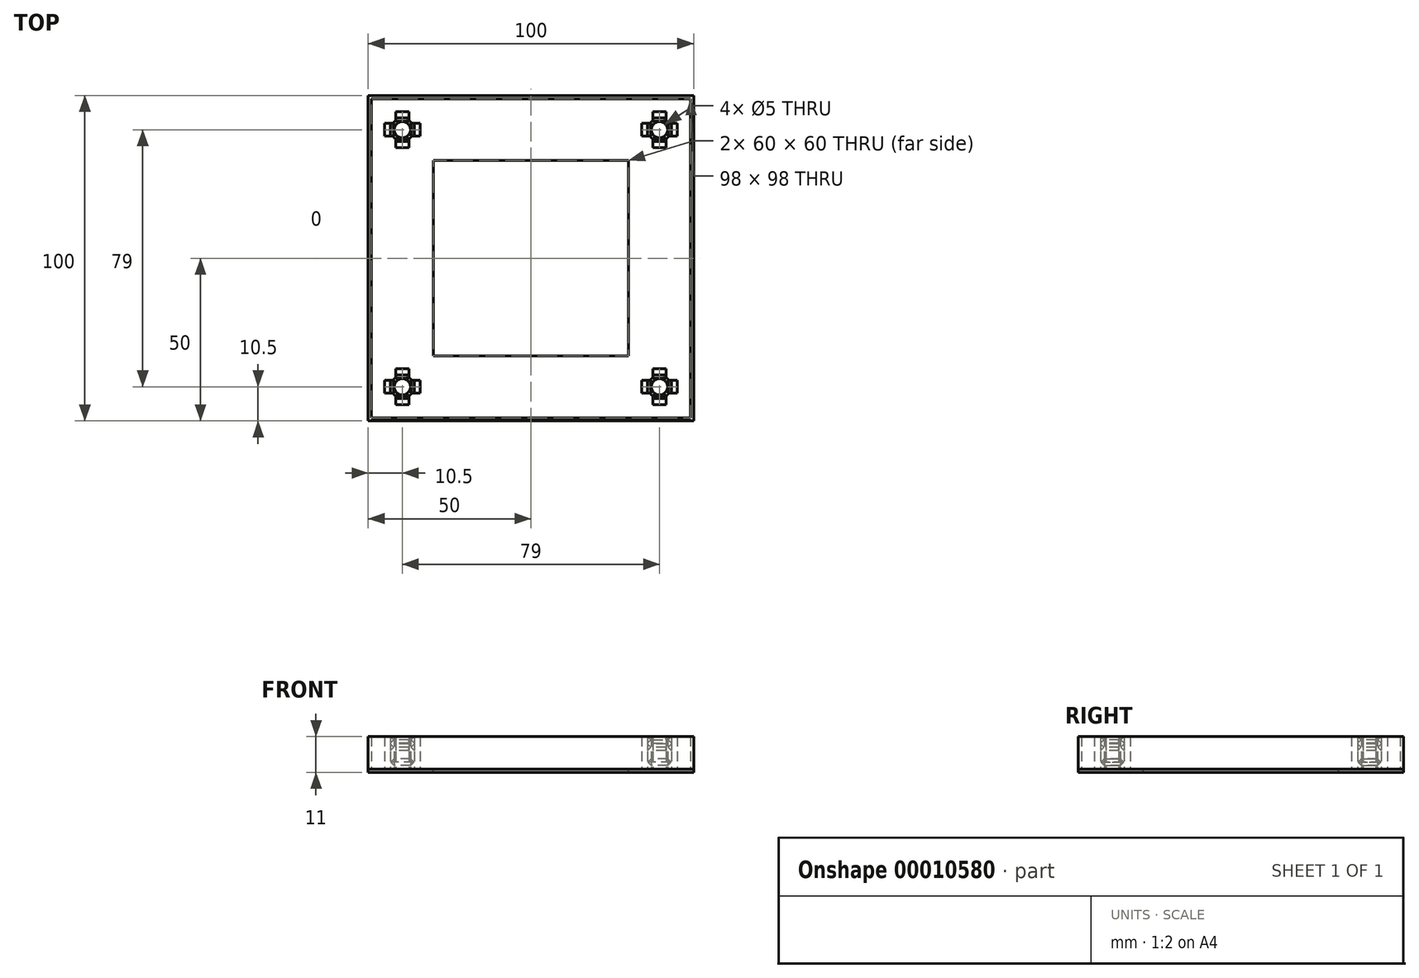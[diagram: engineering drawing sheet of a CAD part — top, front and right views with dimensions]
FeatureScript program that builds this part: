
annotation { "Feature Type Name" : "Feature", "Feature Type Description" : "" }
export const myFeature = defineFeature(function(context is Context, id is Id, definition is map)
    precondition{}
    {
        {
            var Q0;
            Q0=qCreatedBy(makeId("Top.planeOp"),FACE);
            var sketch = newSketch(context, id + "F0", { "sketchPlane" : qUnion([Q0])});
            skLineSegment(sketch, "E0.bottom", {"start": v(-50, 50) * mm, "end": v(50, 50) * mm});
            skLineSegment(sketch, "E0.top", {"start": v(-50, -50) * mm, "end": v(50, -50) * mm});
            skLineSegment(sketch, "E0.left", {"start": v(-50, 50) * mm, "end": v(-50, -50) * mm});
            skLineSegment(sketch, "E0.right", {"start": v(50, 50) * mm, "end": v(50, -50) * mm});
            skCircle(sketch, "E1", {"center": v(-39.5, -39.5) * mm, "radius": 2.5 * mm});
            skCircle(sketch, "E2", {"center": v(-39.5, -39.5) * mm, "radius": 3.5 * mm});
            skLineSegment(sketch, "E3.0", {"start": v(-49, 49) * mm, "end": v(-49, -49) * mm});
            skLineSegment(sketch, "E3.1", {"start": v(-49, 49) * mm, "end": v(49, 49) * mm});
            skLineSegment(sketch, "E3.2", {"start": v(49, 49) * mm, "end": v(49, -49) * mm});
            skLineSegment(sketch, "E3.3", {"start": v(-49, -49) * mm, "end": v(49, -49) * mm});
            skLineSegment(sketch, "E4.0", {"start": v(-30, 30) * mm, "end": v(-30, -30) * mm});
            skLineSegment(sketch, "E4.1", {"start": v(-30, 30) * mm, "end": v(30, 30) * mm});
            skLineSegment(sketch, "E4.2", {"start": v(30, 30) * mm, "end": v(30, -30) * mm});
            skLineSegment(sketch, "E4.3", {"start": v(-30, -30) * mm, "end": v(30, -30) * mm});
            skLineSegment(sketch, "E5", {"start": v(-30, -30) * mm, "end": v(-49, -49) * mm, "construction": true});
            skCircle(sketch, "E6.1.0", {"center": v(39.5, -39.5) * mm, "radius": 2.5 * mm});
            skCircle(sketch, "E6.1.1", {"center": v(39.5, -39.5) * mm, "radius": 3.5 * mm});
            skCircle(sketch, "E6.2.0", {"center": v(39.5, 39.5) * mm, "radius": 2.5 * mm});
            skCircle(sketch, "E6.2.1", {"center": v(39.5, 39.5) * mm, "radius": 3.5 * mm});
            skCircle(sketch, "E6.3.0", {"center": v(-39.5, 39.5) * mm, "radius": 2.5 * mm});
            skCircle(sketch, "E6.3.1", {"center": v(-39.5, 39.5) * mm, "radius": 3.5 * mm});
            skPoint(sketch, "E6.center", {"position": v(0, 0) * mm});
            skSolve(sketch);
        }
        {
            var Q0;
            Q0=makeQuery(id+"F0.imprint","IMPRINT",FACE,{"disambiguationData":[TD([[makeQuery(id+"F0.imprint","IMPRINT",EDGE,{"derivedFrom":sQuery(id+"F0.wireOp",EDGE,"E1")}),1.0]])]});
            var Q1;
            Q1=makeQuery(id+"F0.imprint","IMPRINT",FACE,{"disambiguationData":[TD([[makeQuery(id+"F0.imprint","IMPRINT",EDGE,{"derivedFrom":sQuery(id+"F0.wireOp",EDGE,"E6.3.0")}),1.0]])]});
            var Q2;
            Q2=makeQuery(id+"F0.imprint","IMPRINT",FACE,{"disambiguationData":[TD([[makeQuery(id+"F0.imprint","IMPRINT",EDGE,{"derivedFrom":sQuery(id+"F0.wireOp",EDGE,"E6.2.0")}),1.0]])]});
            var Q3;
            Q3=makeQuery(id+"F0.imprint","IMPRINT",FACE,{"disambiguationData":[TD([[makeQuery(id+"F0.imprint","IMPRINT",EDGE,{"derivedFrom":sQuery(id+"F0.wireOp",EDGE,"E6.1.0")}),1.0]])]});
            extrude(context, id + "F1", {"entities" : qUnion([Q0, Q1, Q2, Q3]), "depth" : 10 * mm});
        }
        {
            var Q0;
            Q0=makeQuery(id+"F0.imprint","IMPRINT",FACE,{"disambiguationData":[TD([[makeQuery(id+"F0.imprint","IMPRINT",EDGE,{"derivedFrom":sQuery(id+"F0.wireOp",EDGE,"E1")}),-1.0]])]});
            var Q1;
            Q1=makeQuery(id+"F0.imprint","IMPRINT",FACE,{"disambiguationData":[TD([[makeQuery(id+"F0.imprint","IMPRINT",EDGE,{"derivedFrom":sQuery(id+"F0.wireOp",EDGE,"E6.3.0")}),-1.0]])]});
            var Q2;
            Q2=makeQuery(id+"F0.imprint","IMPRINT",FACE,{"disambiguationData":[TD([[makeQuery(id+"F0.imprint","IMPRINT",EDGE,{"derivedFrom":sQuery(id+"F0.wireOp",EDGE,"E6.2.0")}),-1.0]])]});
            var Q3;
            Q3=makeQuery(id+"F0.imprint","IMPRINT",FACE,{"disambiguationData":[TD([[makeQuery(id+"F0.imprint","IMPRINT",EDGE,{"derivedFrom":sQuery(id+"F0.wireOp",EDGE,"E6.1.0")}),-1.0]])]});
            extrude(context, id + "F2", {"entities" : qUnion([Q0, Q1, Q2, Q3]), "depth" : 3.15 * mm, "hasSecondDirection" : true, "secondDirectionOppositeDirection" : false, "secondDirectionDepth" : 1.15 * mm});
        }
        {
            var Q0;
            Q0=makeQuery(id+"F2.opExtrude","CAP_EDGE",EDGE,{"disambiguationData":[OSD([sQuery(id+"F0.wireOp",EDGE,"E2")])],"isStart":false});
            var Q1;
            Q1=makeQuery(id+"F2.opExtrude","CAP_EDGE",EDGE,{"disambiguationData":[OSD([sQuery(id+"F0.wireOp",EDGE,"E2")])],"isStart":true});
            var Q2;
            Q2=makeQuery(id+"F2.opExtrude","CAP_EDGE",EDGE,{"disambiguationData":[OSD([sQuery(id+"F0.wireOp",EDGE,"E6.1.1")])],"isStart":true});
            var Q3;
            Q3=makeQuery(id+"F2.opExtrude","CAP_EDGE",EDGE,{"disambiguationData":[OSD([sQuery(id+"F0.wireOp",EDGE,"E6.1.1")])],"isStart":false});
            var Q4;
            Q4=makeQuery(id+"F2.opExtrude","CAP_EDGE",EDGE,{"disambiguationData":[OSD([sQuery(id+"F0.wireOp",EDGE,"E6.3.1")])],"isStart":true});
            var Q5;
            Q5=makeQuery(id+"F2.opExtrude","CAP_EDGE",EDGE,{"disambiguationData":[OSD([sQuery(id+"F0.wireOp",EDGE,"E6.3.1")])],"isStart":false});
            var Q6;
            Q6=makeQuery(id+"F2.opExtrude","CAP_EDGE",EDGE,{"disambiguationData":[OSD([sQuery(id+"F0.wireOp",EDGE,"E6.2.1")])],"isStart":true});
            var Q7;
            Q7=makeQuery(id+"F2.opExtrude","CAP_EDGE",EDGE,{"disambiguationData":[OSD([sQuery(id+"F0.wireOp",EDGE,"E6.2.1")])],"isStart":false});
            chamfer(context, id + "F3", {"entities" : qUnion([Q0, Q1, Q2, Q3, Q4, Q5, Q6, Q7]), "width" : 1 * mm, "tangentPropagation" : true});
        }
        {
            var Q0;
            Q0=makeQuery(id+"F0.imprint","IMPRINT",FACE,{"disambiguationData":[TD([[makeQuery(id+"F0.imprint","IMPRINT",EDGE,{"derivedFrom":sQuery(id+"F0.wireOp",EDGE,"E0.bottom")}),-1.0]])]});
            var Q1;
            Q1=makeQuery(id+"F0.imprint","IMPRINT",FACE,{"disambiguationData":[TD([[makeQuery(id+"F0.imprint","IMPRINT",EDGE,{"derivedFrom":sQuery(id+"F0.wireOp",EDGE,"E1")}),1.0]])]});
            extrude(context, id + "F4", {"entities" : qUnion([Q0, Q1]), "depth" : 10 * mm});
        }
        {
            var Q0;
            Q0=qCreatedBy(makeId("Top.planeOp"),FACE);
            var sketch = newSketch(context, id + "F5", { "sketchPlane" : qUnion([Q0])});
            skLineSegment(sketch, "E7.bottom", {"start": v(50, 50) * mm, "end": v(-50, 50) * mm});
            skLineSegment(sketch, "E7.top", {"start": v(50, -50) * mm, "end": v(-50, -50) * mm});
            skLineSegment(sketch, "E7.left", {"start": v(50, 50) * mm, "end": v(50, -50) * mm});
            skLineSegment(sketch, "E7.right", {"start": v(-50, 50) * mm, "end": v(-50, -50) * mm});
            skLineSegment(sketch, "E8.bottom", {"start": v(-41.5, -34) * mm, "end": v(-37.5, -34) * mm});
            skLineSegment(sketch, "E8.top", {"start": v(-41.5, -37) * mm, "end": v(-37.5, -37) * mm});
            skLineSegment(sketch, "E8.left", {"start": v(-41.5, -34) * mm, "end": v(-41.5, -37) * mm});
            skLineSegment(sketch, "E8.right", {"start": v(-37.5, -34) * mm, "end": v(-37.5, -37) * mm});
            skPoint(sketch, "E9", {"position": v(-39.5, -39.5) * mm});
            skCircle(sketch, "E10", {"center": v(-39.5, -39.5) * mm, "radius": 2.5 * mm, "construction": true});
            skLineSegment(sketch, "E11", {"start": v(-39.5, -39.5) * mm, "end": v(-39.5, -34) * mm, "construction": true});
            skLineSegment(sketch, "E12.1.0", {"start": v(-42, -41.5) * mm, "end": v(-42, -37.5) * mm});
            skLineSegment(sketch, "E12.1.1", {"start": v(-45, -41.5) * mm, "end": v(-45, -37.5) * mm});
            skLineSegment(sketch, "E12.1.2", {"start": v(-45, -37.5) * mm, "end": v(-42, -37.5) * mm});
            skLineSegment(sketch, "E12.1.3", {"start": v(-45, -41.5) * mm, "end": v(-42, -41.5) * mm});
            skLineSegment(sketch, "E12.2.0", {"start": v(-37.5, -42) * mm, "end": v(-41.5, -42) * mm});
            skLineSegment(sketch, "E12.2.1", {"start": v(-37.5, -45) * mm, "end": v(-41.5, -45) * mm});
            skLineSegment(sketch, "E12.2.2", {"start": v(-41.5, -45) * mm, "end": v(-41.5, -42) * mm});
            skLineSegment(sketch, "E12.2.3", {"start": v(-37.5, -45) * mm, "end": v(-37.5, -42) * mm});
            skLineSegment(sketch, "E12.3.0", {"start": v(-37, -37.5) * mm, "end": v(-37, -41.5) * mm});
            skLineSegment(sketch, "E12.3.1", {"start": v(-34, -37.5) * mm, "end": v(-34, -41.5) * mm});
            skLineSegment(sketch, "E12.3.2", {"start": v(-34, -41.5) * mm, "end": v(-37, -41.5) * mm});
            skLineSegment(sketch, "E12.3.3", {"start": v(-34, -37.5) * mm, "end": v(-37, -37.5) * mm});
            skLineSegment(sketch, "E13", {"start": v(-37.5, -35.85) * mm, "end": v(-41.5, -35.85) * mm});
            skLineSegment(sketch, "E14.1.0", {"start": v(-43.15, -37.5) * mm, "end": v(-43.15, -41.5) * mm});
            skLineSegment(sketch, "E14.2.0", {"start": v(-41.5, -43.15) * mm, "end": v(-37.5, -43.15) * mm});
            skLineSegment(sketch, "E14.3.0", {"start": v(-35.85, -41.5) * mm, "end": v(-35.85, -37.5) * mm});
            skLineSegment(sketch, "E15", {"start": v(-41.5, -36.85) * mm, "end": v(-37.5, -36.85) * mm});
            skLineSegment(sketch, "E16.1.0", {"start": v(-42.15, -41.5) * mm, "end": v(-42.15, -37.5) * mm});
            skLineSegment(sketch, "E16.2.0", {"start": v(-37.5, -42.15) * mm, "end": v(-41.5, -42.15) * mm});
            skLineSegment(sketch, "E16.3.0", {"start": v(-36.85, -37.5) * mm, "end": v(-36.85, -41.5) * mm});
            skPoint(sketch, "E17.1.0", {"position": v(39.5, -39.5) * mm});
            skLineSegment(sketch, "E17.1.1", {"start": v(41.5, -45) * mm, "end": v(37.5, -45) * mm});
            skLineSegment(sketch, "E17.1.2", {"start": v(37, -41.5) * mm, "end": v(37, -37.5) * mm});
            skLineSegment(sketch, "E17.1.3", {"start": v(37.5, -37) * mm, "end": v(41.5, -37) * mm});
            skLineSegment(sketch, "E17.1.4", {"start": v(35.85, -37.5) * mm, "end": v(35.85, -41.5) * mm});
            skLineSegment(sketch, "E17.1.5", {"start": v(45, -41.5) * mm, "end": v(42, -41.5) * mm});
            skLineSegment(sketch, "E17.1.6", {"start": v(37.5, -34) * mm, "end": v(37.5, -37) * mm});
            skLineSegment(sketch, "E17.1.7", {"start": v(34, -41.5) * mm, "end": v(34, -37.5) * mm});
            skLineSegment(sketch, "E17.1.8", {"start": v(41.5, -45) * mm, "end": v(41.5, -42) * mm});
            skLineSegment(sketch, "E17.1.9", {"start": v(37.5, -36.85) * mm, "end": v(41.5, -36.85) * mm});
            skLineSegment(sketch, "E17.1.10", {"start": v(34, -37.5) * mm, "end": v(37, -37.5) * mm});
            skLineSegment(sketch, "E17.1.11", {"start": v(45, -37.5) * mm, "end": v(45, -41.5) * mm});
            skLineSegment(sketch, "E17.1.12", {"start": v(36.85, -41.5) * mm, "end": v(36.85, -37.5) * mm});
            skLineSegment(sketch, "E17.1.13", {"start": v(45, -37.5) * mm, "end": v(42, -37.5) * mm});
            skLineSegment(sketch, "E17.1.14", {"start": v(43.15, -41.5) * mm, "end": v(43.15, -37.5) * mm});
            skLineSegment(sketch, "E17.1.15", {"start": v(34, -41.5) * mm, "end": v(37, -41.5) * mm});
            skCircle(sketch, "E17.1.16", {"center": v(39.5, -39.5) * mm, "radius": 2.5 * mm, "construction": true});
            skLineSegment(sketch, "E17.1.17", {"start": v(41.5, -42) * mm, "end": v(37.5, -42) * mm});
            skLineSegment(sketch, "E17.1.18", {"start": v(42.15, -37.5) * mm, "end": v(42.15, -41.5) * mm});
            skLineSegment(sketch, "E17.1.19", {"start": v(39.5, -39.5) * mm, "end": v(34, -39.5) * mm, "construction": true});
            skLineSegment(sketch, "E17.1.20", {"start": v(37.5, -43.15) * mm, "end": v(41.5, -43.15) * mm});
            skLineSegment(sketch, "E17.1.21", {"start": v(41.5, -42.15) * mm, "end": v(37.5, -42.15) * mm});
            skLineSegment(sketch, "E17.1.22", {"start": v(37.5, -34) * mm, "end": v(41.5, -34) * mm});
            skLineSegment(sketch, "E17.1.23", {"start": v(42, -37.5) * mm, "end": v(42, -41.5) * mm});
            skLineSegment(sketch, "E17.1.24", {"start": v(37.5, -45) * mm, "end": v(37.5, -42) * mm});
            skLineSegment(sketch, "E17.1.25", {"start": v(41.5, -34) * mm, "end": v(41.5, -37) * mm});
            skLineSegment(sketch, "E17.1.26", {"start": v(41.5, -35.85) * mm, "end": v(37.5, -35.85) * mm});
            skPoint(sketch, "E17.1.27", {"position": v(39.5, -39.5) * mm});
            skPoint(sketch, "E17.1.28", {"position": v(39.5, -39.5) * mm});
            skPoint(sketch, "E17.1.29", {"position": v(39.5, -39.5) * mm});
            skPoint(sketch, "E17.2.0", {"position": v(39.5, 39.5) * mm});
            skLineSegment(sketch, "E17.2.1", {"start": v(45, 41.5) * mm, "end": v(45, 37.5) * mm});
            skLineSegment(sketch, "E17.2.2", {"start": v(41.5, 37) * mm, "end": v(37.5, 37) * mm});
            skLineSegment(sketch, "E17.2.3", {"start": v(37, 37.5) * mm, "end": v(37, 41.5) * mm});
            skLineSegment(sketch, "E17.2.4", {"start": v(37.5, 35.85) * mm, "end": v(41.5, 35.85) * mm});
            skLineSegment(sketch, "E17.2.5", {"start": v(41.5, 45) * mm, "end": v(41.5, 42) * mm});
            skLineSegment(sketch, "E17.2.6", {"start": v(34, 37.5) * mm, "end": v(37, 37.5) * mm});
            skLineSegment(sketch, "E17.2.7", {"start": v(41.5, 34) * mm, "end": v(37.5, 34) * mm});
            skLineSegment(sketch, "E17.2.8", {"start": v(45, 41.5) * mm, "end": v(42, 41.5) * mm});
            skLineSegment(sketch, "E17.2.9", {"start": v(36.85, 37.5) * mm, "end": v(36.85, 41.5) * mm});
            skLineSegment(sketch, "E17.2.10", {"start": v(37.5, 34) * mm, "end": v(37.5, 37) * mm});
            skLineSegment(sketch, "E17.2.11", {"start": v(37.5, 45) * mm, "end": v(41.5, 45) * mm});
            skLineSegment(sketch, "E17.2.12", {"start": v(41.5, 36.85) * mm, "end": v(37.5, 36.85) * mm});
            skLineSegment(sketch, "E17.2.13", {"start": v(37.5, 45) * mm, "end": v(37.5, 42) * mm});
            skLineSegment(sketch, "E17.2.14", {"start": v(41.5, 43.15) * mm, "end": v(37.5, 43.15) * mm});
            skLineSegment(sketch, "E17.2.15", {"start": v(41.5, 34) * mm, "end": v(41.5, 37) * mm});
            skCircle(sketch, "E17.2.16", {"center": v(39.5, 39.5) * mm, "radius": 2.5 * mm, "construction": true});
            skLineSegment(sketch, "E17.2.17", {"start": v(42, 41.5) * mm, "end": v(42, 37.5) * mm});
            skLineSegment(sketch, "E17.2.18", {"start": v(37.5, 42.15) * mm, "end": v(41.5, 42.15) * mm});
            skLineSegment(sketch, "E17.2.19", {"start": v(39.5, 39.5) * mm, "end": v(39.5, 34) * mm, "construction": true});
            skLineSegment(sketch, "E17.2.20", {"start": v(43.15, 37.5) * mm, "end": v(43.15, 41.5) * mm});
            skLineSegment(sketch, "E17.2.21", {"start": v(42.15, 41.5) * mm, "end": v(42.15, 37.5) * mm});
            skLineSegment(sketch, "E17.2.22", {"start": v(34, 37.5) * mm, "end": v(34, 41.5) * mm});
            skLineSegment(sketch, "E17.2.23", {"start": v(37.5, 42) * mm, "end": v(41.5, 42) * mm});
            skLineSegment(sketch, "E17.2.24", {"start": v(45, 37.5) * mm, "end": v(42, 37.5) * mm});
            skLineSegment(sketch, "E17.2.25", {"start": v(34, 41.5) * mm, "end": v(37, 41.5) * mm});
            skLineSegment(sketch, "E17.2.26", {"start": v(35.85, 41.5) * mm, "end": v(35.85, 37.5) * mm});
            skPoint(sketch, "E17.2.27", {"position": v(39.5, 39.5) * mm});
            skPoint(sketch, "E17.2.28", {"position": v(39.5, 39.5) * mm});
            skPoint(sketch, "E17.2.29", {"position": v(39.5, 39.5) * mm});
            skPoint(sketch, "E17.3.0", {"position": v(-39.5, 39.5) * mm});
            skLineSegment(sketch, "E17.3.1", {"start": v(-41.5, 45) * mm, "end": v(-37.5, 45) * mm});
            skLineSegment(sketch, "E17.3.2", {"start": v(-37, 41.5) * mm, "end": v(-37, 37.5) * mm});
            skLineSegment(sketch, "E17.3.3", {"start": v(-37.5, 37) * mm, "end": v(-41.5, 37) * mm});
            skLineSegment(sketch, "E17.3.4", {"start": v(-35.85, 37.5) * mm, "end": v(-35.85, 41.5) * mm});
            skLineSegment(sketch, "E17.3.5", {"start": v(-45, 41.5) * mm, "end": v(-42, 41.5) * mm});
            skLineSegment(sketch, "E17.3.6", {"start": v(-37.5, 34) * mm, "end": v(-37.5, 37) * mm});
            skLineSegment(sketch, "E17.3.7", {"start": v(-34, 41.5) * mm, "end": v(-34, 37.5) * mm});
            skLineSegment(sketch, "E17.3.8", {"start": v(-41.5, 45) * mm, "end": v(-41.5, 42) * mm});
            skLineSegment(sketch, "E17.3.9", {"start": v(-37.5, 36.85) * mm, "end": v(-41.5, 36.85) * mm});
            skLineSegment(sketch, "E17.3.10", {"start": v(-34, 37.5) * mm, "end": v(-37, 37.5) * mm});
            skLineSegment(sketch, "E17.3.11", {"start": v(-45, 37.5) * mm, "end": v(-45, 41.5) * mm});
            skLineSegment(sketch, "E17.3.12", {"start": v(-36.85, 41.5) * mm, "end": v(-36.85, 37.5) * mm});
            skLineSegment(sketch, "E17.3.13", {"start": v(-45, 37.5) * mm, "end": v(-42, 37.5) * mm});
            skLineSegment(sketch, "E17.3.14", {"start": v(-43.15, 41.5) * mm, "end": v(-43.15, 37.5) * mm});
            skLineSegment(sketch, "E17.3.15", {"start": v(-34, 41.5) * mm, "end": v(-37, 41.5) * mm});
            skCircle(sketch, "E17.3.16", {"center": v(-39.5, 39.5) * mm, "radius": 2.5 * mm, "construction": true});
            skLineSegment(sketch, "E17.3.17", {"start": v(-41.5, 42) * mm, "end": v(-37.5, 42) * mm});
            skLineSegment(sketch, "E17.3.18", {"start": v(-42.15, 37.5) * mm, "end": v(-42.15, 41.5) * mm});
            skLineSegment(sketch, "E17.3.19", {"start": v(-39.5, 39.5) * mm, "end": v(-34, 39.5) * mm, "construction": true});
            skLineSegment(sketch, "E17.3.20", {"start": v(-37.5, 43.15) * mm, "end": v(-41.5, 43.15) * mm});
            skLineSegment(sketch, "E17.3.21", {"start": v(-41.5, 42.15) * mm, "end": v(-37.5, 42.15) * mm});
            skLineSegment(sketch, "E17.3.22", {"start": v(-37.5, 34) * mm, "end": v(-41.5, 34) * mm});
            skLineSegment(sketch, "E17.3.23", {"start": v(-42, 37.5) * mm, "end": v(-42, 41.5) * mm});
            skLineSegment(sketch, "E17.3.24", {"start": v(-37.5, 45) * mm, "end": v(-37.5, 42) * mm});
            skLineSegment(sketch, "E17.3.25", {"start": v(-41.5, 34) * mm, "end": v(-41.5, 37) * mm});
            skLineSegment(sketch, "E17.3.26", {"start": v(-41.5, 35.85) * mm, "end": v(-37.5, 35.85) * mm});
            skPoint(sketch, "E17.3.27", {"position": v(-39.5, 39.5) * mm});
            skPoint(sketch, "E17.3.28", {"position": v(-39.5, 39.5) * mm});
            skPoint(sketch, "E17.3.29", {"position": v(-39.5, 39.5) * mm});
            skPoint(sketch, "E17.center", {"position": v(0, 0) * mm});
            skLineSegment(sketch, "E18.bottom", {"start": v(-30, 30) * mm, "end": v(30, 30) * mm});
            skLineSegment(sketch, "E18.top", {"start": v(-30, -30) * mm, "end": v(30, -30) * mm});
            skLineSegment(sketch, "E18.left", {"start": v(-30, 30) * mm, "end": v(-30, -30) * mm});
            skLineSegment(sketch, "E18.right", {"start": v(30, 30) * mm, "end": v(30, -30) * mm});
            skSolve(sketch);
        }
        {
            var Q0;
            {var subQ2=sQuery(id+"F5.wireOp",EDGE,"E8.bottom");Q0=makeQuery(id+"F5.imprint","IMPRINT",FACE,{"disambiguationData":[TD([[makeQuery(id+"F5.imprint","IMPRINT",EDGE,{"derivedFrom":subQ2}),-1.0]])]});}
            var Q1;
            {var subQ2=sQuery(id+"F5.wireOp",EDGE,"E12.3.1");Q1=makeQuery(id+"F5.imprint","IMPRINT",FACE,{"disambiguationData":[TD([[makeQuery(id+"F5.imprint","IMPRINT",EDGE,{"derivedFrom":subQ2}),-1.0]])]});}
            var Q2;
            {var subQ2=sQuery(id+"F5.wireOp",EDGE,"E12.2.1");Q2=makeQuery(id+"F5.imprint","IMPRINT",FACE,{"disambiguationData":[TD([[makeQuery(id+"F5.imprint","IMPRINT",EDGE,{"derivedFrom":subQ2}),-1.0]])]});}
            var Q3;
            {var subQ2=sQuery(id+"F5.wireOp",EDGE,"E12.1.1");Q3=makeQuery(id+"F5.imprint","IMPRINT",FACE,{"disambiguationData":[TD([[makeQuery(id+"F5.imprint","IMPRINT",EDGE,{"derivedFrom":subQ2}),-1.0]])]});}
            var Q4;
            {var subQ2=sQuery(id+"F5.wireOp",EDGE,"E17.1.11");Q4=makeQuery(id+"F5.imprint","IMPRINT",FACE,{"disambiguationData":[TD([[makeQuery(id+"F5.imprint","IMPRINT",EDGE,{"derivedFrom":subQ2}),-1.0]])]});}
            var Q5;
            {var subQ2=sQuery(id+"F5.wireOp",EDGE,"E17.1.1");Q5=makeQuery(id+"F5.imprint","IMPRINT",FACE,{"disambiguationData":[TD([[makeQuery(id+"F5.imprint","IMPRINT",EDGE,{"derivedFrom":subQ2}),-1.0]])]});}
            var Q6;
            {var subQ2=sQuery(id+"F5.wireOp",EDGE,"E17.1.4");Q6=makeQuery(id+"F5.imprint","IMPRINT",FACE,{"disambiguationData":[TD([[makeQuery(id+"F5.imprint","IMPRINT",EDGE,{"derivedFrom":subQ2}),-1.0]])]});}
            var Q7;
            {var subQ2=sQuery(id+"F5.wireOp",EDGE,"E17.1.22");Q7=makeQuery(id+"F5.imprint","IMPRINT",FACE,{"disambiguationData":[TD([[makeQuery(id+"F5.imprint","IMPRINT",EDGE,{"derivedFrom":subQ2}),-1.0]])]});}
            var Q8;
            {var subQ2=sQuery(id+"F5.wireOp",EDGE,"E17.2.22");Q8=makeQuery(id+"F5.imprint","IMPRINT",FACE,{"disambiguationData":[TD([[makeQuery(id+"F5.imprint","IMPRINT",EDGE,{"derivedFrom":subQ2}),-1.0]])]});}
            var Q9;
            {var subQ2=sQuery(id+"F5.wireOp",EDGE,"E17.2.11");Q9=makeQuery(id+"F5.imprint","IMPRINT",FACE,{"disambiguationData":[TD([[makeQuery(id+"F5.imprint","IMPRINT",EDGE,{"derivedFrom":subQ2}),-1.0]])]});}
            var Q10;
            {var subQ2=sQuery(id+"F5.wireOp",EDGE,"E17.2.1");Q10=makeQuery(id+"F5.imprint","IMPRINT",FACE,{"disambiguationData":[TD([[makeQuery(id+"F5.imprint","IMPRINT",EDGE,{"derivedFrom":subQ2}),-1.0]])]});}
            var Q11;
            {var subQ2=sQuery(id+"F5.wireOp",EDGE,"E17.2.4");Q11=makeQuery(id+"F5.imprint","IMPRINT",FACE,{"disambiguationData":[TD([[makeQuery(id+"F5.imprint","IMPRINT",EDGE,{"derivedFrom":subQ2}),-1.0]])]});}
            var Q12;
            {var subQ2=sQuery(id+"F5.wireOp",EDGE,"E17.3.1");Q12=makeQuery(id+"F5.imprint","IMPRINT",FACE,{"disambiguationData":[TD([[makeQuery(id+"F5.imprint","IMPRINT",EDGE,{"derivedFrom":subQ2}),-1.0]])]});}
            var Q13;
            {var subQ2=sQuery(id+"F5.wireOp",EDGE,"E17.3.11");Q13=makeQuery(id+"F5.imprint","IMPRINT",FACE,{"disambiguationData":[TD([[makeQuery(id+"F5.imprint","IMPRINT",EDGE,{"derivedFrom":subQ2}),-1.0]])]});}
            var Q14;
            {var subQ1=sQuery(id+"F5.wireOp",EDGE,"E17.3.22");Q14=makeQuery(id+"F5.imprint","IMPRINT",FACE,{"disambiguationData":[TD([[makeQuery(id+"F5.imprint","IMPRINT",EDGE,{"derivedFrom":subQ1}),-1.0]])]});}
            var Q15;
            {var subQ2=sQuery(id+"F5.wireOp",EDGE,"E17.3.4");Q15=makeQuery(id+"F5.imprint","IMPRINT",FACE,{"disambiguationData":[TD([[makeQuery(id+"F5.imprint","IMPRINT",EDGE,{"derivedFrom":subQ2}),-1.0]])]});}
            extrude(context, id + "F6", {"entities" : qUnion([Q0, Q1, Q2, Q3, Q4, Q5, Q6, Q7, Q8, Q9, Q10, Q11, Q12, Q13, Q14, Q15]), "depth" : 10 * mm});
        }
        {
            var Q0;
            {var subQ1=sQuery(id+"F5.wireOp",EDGE,"E14.1.0");Q0=makeQuery(id+"F5.imprint","IMPRINT",FACE,{"disambiguationData":[TD([[makeQuery(id+"F5.imprint","IMPRINT",EDGE,{"derivedFrom":subQ1}),1.0]])]});}
            var Q1;
            {var subQ1=sQuery(id+"F5.wireOp",EDGE,"E13");Q1=makeQuery(id+"F5.imprint","IMPRINT",FACE,{"disambiguationData":[TD([[makeQuery(id+"F5.imprint","IMPRINT",EDGE,{"derivedFrom":subQ1}),1.0]])]});}
            var Q2;
            {var subQ1=sQuery(id+"F5.wireOp",EDGE,"E14.3.0");Q2=makeQuery(id+"F5.imprint","IMPRINT",FACE,{"disambiguationData":[TD([[makeQuery(id+"F5.imprint","IMPRINT",EDGE,{"derivedFrom":subQ1}),1.0]])]});}
            var Q3;
            {var subQ1=sQuery(id+"F5.wireOp",EDGE,"E14.2.0");Q3=makeQuery(id+"F5.imprint","IMPRINT",FACE,{"disambiguationData":[TD([[makeQuery(id+"F5.imprint","IMPRINT",EDGE,{"derivedFrom":subQ1}),1.0]])]});}
            var Q4;
            {var subQ2=sQuery(id+"F5.wireOp",EDGE,"E17.3.4");Q4=makeQuery(id+"F5.imprint","IMPRINT",FACE,{"disambiguationData":[TD([[makeQuery(id+"F5.imprint","IMPRINT",EDGE,{"derivedFrom":subQ2}),1.0]])]});}
            var Q5;
            {var subQ2=sQuery(id+"F5.wireOp",EDGE,"E17.3.9");Q5=makeQuery(id+"F5.imprint","IMPRINT",FACE,{"disambiguationData":[TD([[makeQuery(id+"F5.imprint","IMPRINT",EDGE,{"derivedFrom":subQ2}),1.0]])]});}
            var Q6;
            {var subQ2=sQuery(id+"F5.wireOp",EDGE,"E17.3.20");Q6=makeQuery(id+"F5.imprint","IMPRINT",FACE,{"disambiguationData":[TD([[makeQuery(id+"F5.imprint","IMPRINT",EDGE,{"derivedFrom":subQ2}),1.0]])]});}
            var Q7;
            {var subQ1=sQuery(id+"F5.wireOp",EDGE,"E17.3.14");Q7=makeQuery(id+"F5.imprint","IMPRINT",FACE,{"disambiguationData":[TD([[makeQuery(id+"F5.imprint","IMPRINT",EDGE,{"derivedFrom":subQ1}),1.0]])]});}
            var Q8;
            {var subQ2=sQuery(id+"F5.wireOp",EDGE,"E17.2.9");Q8=makeQuery(id+"F5.imprint","IMPRINT",FACE,{"disambiguationData":[TD([[makeQuery(id+"F5.imprint","IMPRINT",EDGE,{"derivedFrom":subQ2}),1.0]])]});}
            var Q9;
            {var subQ1=sQuery(id+"F5.wireOp",EDGE,"E17.2.14");Q9=makeQuery(id+"F5.imprint","IMPRINT",FACE,{"disambiguationData":[TD([[makeQuery(id+"F5.imprint","IMPRINT",EDGE,{"derivedFrom":subQ1}),1.0]])]});}
            var Q10;
            {var subQ2=sQuery(id+"F5.wireOp",EDGE,"E17.2.4");Q10=makeQuery(id+"F5.imprint","IMPRINT",FACE,{"disambiguationData":[TD([[makeQuery(id+"F5.imprint","IMPRINT",EDGE,{"derivedFrom":subQ2}),1.0]])]});}
            var Q11;
            {var subQ2=sQuery(id+"F5.wireOp",EDGE,"E17.2.20");Q11=makeQuery(id+"F5.imprint","IMPRINT",FACE,{"disambiguationData":[TD([[makeQuery(id+"F5.imprint","IMPRINT",EDGE,{"derivedFrom":subQ2}),1.0]])]});}
            var Q12;
            {var subQ2=sQuery(id+"F5.wireOp",EDGE,"E17.1.4");Q12=makeQuery(id+"F5.imprint","IMPRINT",FACE,{"disambiguationData":[TD([[makeQuery(id+"F5.imprint","IMPRINT",EDGE,{"derivedFrom":subQ2}),1.0]])]});}
            var Q13;
            {var subQ2=sQuery(id+"F5.wireOp",EDGE,"E17.1.9");Q13=makeQuery(id+"F5.imprint","IMPRINT",FACE,{"disambiguationData":[TD([[makeQuery(id+"F5.imprint","IMPRINT",EDGE,{"derivedFrom":subQ2}),1.0]])]});}
            var Q14;
            {var subQ2=sQuery(id+"F5.wireOp",EDGE,"E17.1.14");Q14=makeQuery(id+"F5.imprint","IMPRINT",FACE,{"disambiguationData":[TD([[makeQuery(id+"F5.imprint","IMPRINT",EDGE,{"derivedFrom":subQ2}),1.0]])]});}
            var Q15;
            {var subQ2=sQuery(id+"F5.wireOp",EDGE,"E17.1.20");Q15=makeQuery(id+"F5.imprint","IMPRINT",FACE,{"disambiguationData":[TD([[makeQuery(id+"F5.imprint","IMPRINT",EDGE,{"derivedFrom":subQ2}),1.0]])]});}
            extrude(context, id + "F7", {"entities" : qUnion([Q0, Q1, Q2, Q3, Q4, Q5, Q6, Q7, Q8, Q9, Q10, Q11, Q12, Q13, Q14, Q15]), "depth" : 7.7 * mm, "hasSecondDirection" : true, "secondDirectionOppositeDirection" : false, "secondDirectionDepth" : 5.7 * mm});
        }
        {
            var Q0;
            Q0=makeQuery(id+"F7.opExtrude","CAP_EDGE",EDGE,{"disambiguationData":[OSD([sQuery(id+"F5.wireOp",EDGE,"E16.1.0")])],"isStart":false});
            var Q1;
            Q1=makeQuery(id+"F7.opExtrude","CAP_EDGE",EDGE,{"disambiguationData":[OSD([sQuery(id+"F5.wireOp",EDGE,"E15")])],"isStart":false});
            var Q2;
            Q2=makeQuery(id+"F7.opExtrude","CAP_EDGE",EDGE,{"disambiguationData":[OSD([sQuery(id+"F5.wireOp",EDGE,"E15")])],"isStart":true});
            var Q3;
            Q3=makeQuery(id+"F7.opExtrude","CAP_EDGE",EDGE,{"disambiguationData":[OSD([sQuery(id+"F5.wireOp",EDGE,"E16.1.0")])],"isStart":true});
            var Q4;
            Q4=makeQuery(id+"F7.opExtrude","CAP_EDGE",EDGE,{"disambiguationData":[OSD([sQuery(id+"F5.wireOp",EDGE,"E16.3.0")])],"isStart":true});
            var Q5;
            Q5=makeQuery(id+"F7.opExtrude","CAP_EDGE",EDGE,{"disambiguationData":[OSD([sQuery(id+"F5.wireOp",EDGE,"E16.3.0")])],"isStart":false});
            var Q6;
            Q6=makeQuery(id+"F7.opExtrude","CAP_EDGE",EDGE,{"disambiguationData":[OSD([sQuery(id+"F5.wireOp",EDGE,"E16.2.0")])],"isStart":true});
            var Q7;
            Q7=makeQuery(id+"F7.opExtrude","CAP_EDGE",EDGE,{"disambiguationData":[OSD([sQuery(id+"F5.wireOp",EDGE,"E16.2.0")])],"isStart":false});
            var Q8;
            Q8=makeQuery(id+"F7.opExtrude","CAP_EDGE",EDGE,{"disambiguationData":[OSD([sQuery(id+"F5.wireOp",EDGE,"E17.1.9")])],"isStart":false});
            var Q9;
            Q9=makeQuery(id+"F7.opExtrude","CAP_EDGE",EDGE,{"disambiguationData":[OSD([sQuery(id+"F5.wireOp",EDGE,"E17.1.12")])],"isStart":false});
            var Q10;
            Q10=makeQuery(id+"F7.opExtrude","CAP_EDGE",EDGE,{"disambiguationData":[OSD([sQuery(id+"F5.wireOp",EDGE,"E17.1.21")])],"isStart":false});
            var Q11;
            Q11=makeQuery(id+"F7.opExtrude","CAP_EDGE",EDGE,{"disambiguationData":[OSD([sQuery(id+"F5.wireOp",EDGE,"E17.1.18")])],"isStart":false});
            var Q12;
            Q12=makeQuery(id+"F7.opExtrude","CAP_EDGE",EDGE,{"disambiguationData":[OSD([sQuery(id+"F5.wireOp",EDGE,"E17.1.9")])],"isStart":true});
            var Q13;
            Q13=makeQuery(id+"F7.opExtrude","CAP_EDGE",EDGE,{"disambiguationData":[OSD([sQuery(id+"F5.wireOp",EDGE,"E17.1.18")])],"isStart":true});
            var Q14;
            Q14=makeQuery(id+"F7.opExtrude","CAP_EDGE",EDGE,{"disambiguationData":[OSD([sQuery(id+"F5.wireOp",EDGE,"E17.1.12")])],"isStart":true});
            var Q15;
            Q15=makeQuery(id+"F7.opExtrude","CAP_EDGE",EDGE,{"disambiguationData":[OSD([sQuery(id+"F5.wireOp",EDGE,"E17.1.21")])],"isStart":true});
            var Q16;
            Q16=makeQuery(id+"F7.opExtrude","CAP_EDGE",EDGE,{"disambiguationData":[OSD([sQuery(id+"F5.wireOp",EDGE,"E17.3.18")])],"isStart":false});
            var Q17;
            Q17=makeQuery(id+"F7.opExtrude","CAP_EDGE",EDGE,{"disambiguationData":[OSD([sQuery(id+"F5.wireOp",EDGE,"E17.3.18")])],"isStart":true});
            var Q18;
            Q18=makeQuery(id+"F7.opExtrude","CAP_EDGE",EDGE,{"disambiguationData":[OSD([sQuery(id+"F5.wireOp",EDGE,"E17.3.12")])],"isStart":false});
            var Q19;
            Q19=makeQuery(id+"F7.opExtrude","CAP_EDGE",EDGE,{"disambiguationData":[OSD([sQuery(id+"F5.wireOp",EDGE,"E17.3.21")])],"isStart":false});
            var Q20;
            Q20=makeQuery(id+"F7.opExtrude","CAP_EDGE",EDGE,{"disambiguationData":[OSD([sQuery(id+"F5.wireOp",EDGE,"E17.2.18")])],"isStart":false});
            var Q21;
            Q21=makeQuery(id+"F7.opExtrude","CAP_EDGE",EDGE,{"disambiguationData":[OSD([sQuery(id+"F5.wireOp",EDGE,"E17.2.18")])],"isStart":true});
            var Q22;
            Q22=makeQuery(id+"F7.opExtrude","CAP_EDGE",EDGE,{"disambiguationData":[OSD([sQuery(id+"F5.wireOp",EDGE,"E17.2.21")])],"isStart":false});
            var Q23;
            Q23=makeQuery(id+"F7.opExtrude","CAP_EDGE",EDGE,{"disambiguationData":[OSD([sQuery(id+"F5.wireOp",EDGE,"E17.2.9")])],"isStart":false});
            var Q24;
            Q24=makeQuery(id+"F7.opExtrude","CAP_EDGE",EDGE,{"disambiguationData":[OSD([sQuery(id+"F5.wireOp",EDGE,"E17.2.9")])],"isStart":true});
            var Q25;
            Q25=makeQuery(id+"F7.opExtrude","CAP_EDGE",EDGE,{"disambiguationData":[OSD([sQuery(id+"F5.wireOp",EDGE,"E17.2.12")])],"isStart":false});
            var Q26;
            Q26=makeQuery(id+"F7.opExtrude","CAP_EDGE",EDGE,{"disambiguationData":[OSD([sQuery(id+"F5.wireOp",EDGE,"E17.3.12")])],"isStart":true});
            var Q27;
            Q27=makeQuery(id+"F7.opExtrude","CAP_EDGE",EDGE,{"disambiguationData":[OSD([sQuery(id+"F5.wireOp",EDGE,"E17.3.9")])],"isStart":true});
            var Q28;
            Q28=makeQuery(id+"F7.opExtrude","CAP_EDGE",EDGE,{"disambiguationData":[OSD([sQuery(id+"F5.wireOp",EDGE,"E17.3.21")])],"isStart":true});
            var Q29;
            Q29=makeQuery(id+"F7.opExtrude","CAP_EDGE",EDGE,{"disambiguationData":[OSD([sQuery(id+"F5.wireOp",EDGE,"E17.2.12")])],"isStart":true});
            var Q30;
            Q30=makeQuery(id+"F7.opExtrude","CAP_EDGE",EDGE,{"disambiguationData":[OSD([sQuery(id+"F5.wireOp",EDGE,"E17.2.21")])],"isStart":true});
            var Q31;
            Q31=makeQuery(id+"F7.opExtrude","CAP_EDGE",EDGE,{"disambiguationData":[OSD([sQuery(id+"F5.wireOp",EDGE,"E17.3.9")])],"isStart":false});
            chamfer(context, id + "F8", {"entities" : qUnion([Q0, Q1, Q2, Q3, Q4, Q5, Q6, Q7, Q8, Q9, Q10, Q11, Q12, Q13, Q14, Q15, Q16, Q17, Q18, Q19, Q20, Q21, Q22, Q23, Q24, Q25, Q26, Q27, Q28, Q29, Q30, Q31]), "width" : 1 * mm, "tangentPropagation" : true});
        }
        {
            var Q0;
            {var subQ1=sQuery(id+"F5.wireOp",EDGE,"E14.1.0");Q0=makeQuery(id+"F5.imprint","IMPRINT",FACE,{"disambiguationData":[TD([[makeQuery(id+"F5.imprint","IMPRINT",EDGE,{"derivedFrom":subQ1}),1.0]])]});}
            var Q1;
            {var subQ1=sQuery(id+"F5.wireOp",EDGE,"E14.3.0");Q1=makeQuery(id+"F5.imprint","IMPRINT",FACE,{"disambiguationData":[TD([[makeQuery(id+"F5.imprint","IMPRINT",EDGE,{"derivedFrom":subQ1}),1.0]])]});}
            var Q2;
            {var subQ1=sQuery(id+"F5.wireOp",EDGE,"E14.2.0");Q2=makeQuery(id+"F5.imprint","IMPRINT",FACE,{"disambiguationData":[TD([[makeQuery(id+"F5.imprint","IMPRINT",EDGE,{"derivedFrom":subQ1}),1.0]])]});}
            var Q3;
            {var subQ1=sQuery(id+"F5.wireOp",EDGE,"E13");Q3=makeQuery(id+"F5.imprint","IMPRINT",FACE,{"disambiguationData":[TD([[makeQuery(id+"F5.imprint","IMPRINT",EDGE,{"derivedFrom":subQ1}),1.0]])]});}
            var Q4;
            {var subQ2=sQuery(id+"F5.wireOp",EDGE,"E17.1.20");Q4=makeQuery(id+"F5.imprint","IMPRINT",FACE,{"disambiguationData":[TD([[makeQuery(id+"F5.imprint","IMPRINT",EDGE,{"derivedFrom":subQ2}),1.0]])]});}
            var Q5;
            {var subQ2=sQuery(id+"F5.wireOp",EDGE,"E17.1.4");Q5=makeQuery(id+"F5.imprint","IMPRINT",FACE,{"disambiguationData":[TD([[makeQuery(id+"F5.imprint","IMPRINT",EDGE,{"derivedFrom":subQ2}),1.0]])]});}
            var Q6;
            {var subQ2=sQuery(id+"F5.wireOp",EDGE,"E17.1.9");Q6=makeQuery(id+"F5.imprint","IMPRINT",FACE,{"disambiguationData":[TD([[makeQuery(id+"F5.imprint","IMPRINT",EDGE,{"derivedFrom":subQ2}),1.0]])]});}
            var Q7;
            {var subQ2=sQuery(id+"F5.wireOp",EDGE,"E17.1.14");Q7=makeQuery(id+"F5.imprint","IMPRINT",FACE,{"disambiguationData":[TD([[makeQuery(id+"F5.imprint","IMPRINT",EDGE,{"derivedFrom":subQ2}),1.0]])]});}
            var Q8;
            {var subQ2=sQuery(id+"F5.wireOp",EDGE,"E17.2.20");Q8=makeQuery(id+"F5.imprint","IMPRINT",FACE,{"disambiguationData":[TD([[makeQuery(id+"F5.imprint","IMPRINT",EDGE,{"derivedFrom":subQ2}),1.0]])]});}
            var Q9;
            {var subQ2=sQuery(id+"F5.wireOp",EDGE,"E17.2.4");Q9=makeQuery(id+"F5.imprint","IMPRINT",FACE,{"disambiguationData":[TD([[makeQuery(id+"F5.imprint","IMPRINT",EDGE,{"derivedFrom":subQ2}),1.0]])]});}
            var Q10;
            {var subQ2=sQuery(id+"F5.wireOp",EDGE,"E17.2.9");Q10=makeQuery(id+"F5.imprint","IMPRINT",FACE,{"disambiguationData":[TD([[makeQuery(id+"F5.imprint","IMPRINT",EDGE,{"derivedFrom":subQ2}),1.0]])]});}
            var Q11;
            {var subQ1=sQuery(id+"F5.wireOp",EDGE,"E17.2.14");Q11=makeQuery(id+"F5.imprint","IMPRINT",FACE,{"disambiguationData":[TD([[makeQuery(id+"F5.imprint","IMPRINT",EDGE,{"derivedFrom":subQ1}),1.0]])]});}
            var Q12;
            {var subQ2=sQuery(id+"F5.wireOp",EDGE,"E17.3.9");Q12=makeQuery(id+"F5.imprint","IMPRINT",FACE,{"disambiguationData":[TD([[makeQuery(id+"F5.imprint","IMPRINT",EDGE,{"derivedFrom":subQ2}),1.0]])]});}
            var Q13;
            {var subQ1=sQuery(id+"F5.wireOp",EDGE,"E17.3.14");Q13=makeQuery(id+"F5.imprint","IMPRINT",FACE,{"disambiguationData":[TD([[makeQuery(id+"F5.imprint","IMPRINT",EDGE,{"derivedFrom":subQ1}),1.0]])]});}
            var Q14;
            {var subQ2=sQuery(id+"F5.wireOp",EDGE,"E17.3.20");Q14=makeQuery(id+"F5.imprint","IMPRINT",FACE,{"disambiguationData":[TD([[makeQuery(id+"F5.imprint","IMPRINT",EDGE,{"derivedFrom":subQ2}),1.0]])]});}
            var Q15;
            {var subQ2=sQuery(id+"F5.wireOp",EDGE,"E17.3.4");Q15=makeQuery(id+"F5.imprint","IMPRINT",FACE,{"disambiguationData":[TD([[makeQuery(id+"F5.imprint","IMPRINT",EDGE,{"derivedFrom":subQ2}),1.0]])]});}
            extrude(context, id + "F9", {"entities" : qUnion([Q0, Q1, Q2, Q3, Q4, Q5, Q6, Q7, Q8, Q9, Q10, Q11, Q12, Q13, Q14, Q15]), "depth" : 10 * mm, "hasSecondDirection" : true, "secondDirectionOppositeDirection" : false, "secondDirectionDepth" : 8 * mm});
        }
        {
            var Q0;
            Q0=makeQuery(id+"F9.opExtrude","CAP_EDGE",EDGE,{"disambiguationData":[OSD([sQuery(id+"F5.wireOp",EDGE,"E16.1.0")])],"isStart":false});
            var Q1;
            Q1=makeQuery(id+"F9.opExtrude","CAP_EDGE",EDGE,{"disambiguationData":[OSD([sQuery(id+"F5.wireOp",EDGE,"E15")])],"isStart":false});
            var Q2;
            Q2=makeQuery(id+"F9.opExtrude","CAP_EDGE",EDGE,{"disambiguationData":[OSD([sQuery(id+"F5.wireOp",EDGE,"E16.3.0")])],"isStart":false});
            var Q3;
            Q3=makeQuery(id+"F9.opExtrude","CAP_EDGE",EDGE,{"disambiguationData":[OSD([sQuery(id+"F5.wireOp",EDGE,"E16.3.0")])],"isStart":true});
            var Q4;
            Q4=makeQuery(id+"F9.opExtrude","CAP_EDGE",EDGE,{"disambiguationData":[OSD([sQuery(id+"F5.wireOp",EDGE,"E15")])],"isStart":true});
            var Q5;
            Q5=makeQuery(id+"F9.opExtrude","CAP_EDGE",EDGE,{"disambiguationData":[OSD([sQuery(id+"F5.wireOp",EDGE,"E16.1.0")])],"isStart":true});
            var Q6;
            Q6=makeQuery(id+"F9.opExtrude","CAP_EDGE",EDGE,{"disambiguationData":[OSD([sQuery(id+"F5.wireOp",EDGE,"E16.2.0")])],"isStart":true});
            var Q7;
            Q7=makeQuery(id+"F9.opExtrude","CAP_EDGE",EDGE,{"disambiguationData":[OSD([sQuery(id+"F5.wireOp",EDGE,"E16.2.0")])],"isStart":false});
            var Q8;
            Q8=makeQuery(id+"F9.opExtrude","CAP_EDGE",EDGE,{"disambiguationData":[OSD([sQuery(id+"F5.wireOp",EDGE,"E17.3.9")])],"isStart":false});
            var Q9;
            Q9=makeQuery(id+"F9.opExtrude","CAP_EDGE",EDGE,{"disambiguationData":[OSD([sQuery(id+"F5.wireOp",EDGE,"E17.3.9")])],"isStart":true});
            var Q10;
            Q10=makeQuery(id+"F9.opExtrude","CAP_EDGE",EDGE,{"disambiguationData":[OSD([sQuery(id+"F5.wireOp",EDGE,"E17.3.18")])],"isStart":true});
            var Q11;
            Q11=makeQuery(id+"F9.opExtrude","CAP_EDGE",EDGE,{"disambiguationData":[OSD([sQuery(id+"F5.wireOp",EDGE,"E17.3.18")])],"isStart":false});
            var Q12;
            Q12=makeQuery(id+"F9.opExtrude","CAP_EDGE",EDGE,{"disambiguationData":[OSD([sQuery(id+"F5.wireOp",EDGE,"E17.3.21")])],"isStart":false});
            var Q13;
            Q13=makeQuery(id+"F9.opExtrude","CAP_EDGE",EDGE,{"disambiguationData":[OSD([sQuery(id+"F5.wireOp",EDGE,"E17.3.12")])],"isStart":false});
            var Q14;
            Q14=makeQuery(id+"F9.opExtrude","CAP_EDGE",EDGE,{"disambiguationData":[OSD([sQuery(id+"F5.wireOp",EDGE,"E17.1.12")])],"isStart":true});
            var Q15;
            Q15=makeQuery(id+"F9.opExtrude","CAP_EDGE",EDGE,{"disambiguationData":[OSD([sQuery(id+"F5.wireOp",EDGE,"E17.1.12")])],"isStart":false});
            var Q16;
            Q16=makeQuery(id+"F9.opExtrude","CAP_EDGE",EDGE,{"disambiguationData":[OSD([sQuery(id+"F5.wireOp",EDGE,"E17.1.18")])],"isStart":false});
            var Q17;
            Q17=makeQuery(id+"F9.opExtrude","CAP_EDGE",EDGE,{"disambiguationData":[OSD([sQuery(id+"F5.wireOp",EDGE,"E17.1.21")])],"isStart":false});
            var Q18;
            Q18=makeQuery(id+"F9.opExtrude","CAP_EDGE",EDGE,{"disambiguationData":[OSD([sQuery(id+"F5.wireOp",EDGE,"E17.1.9")])],"isStart":false});
            var Q19;
            Q19=makeQuery(id+"F9.opExtrude","CAP_EDGE",EDGE,{"disambiguationData":[OSD([sQuery(id+"F5.wireOp",EDGE,"E17.2.12")])],"isStart":false});
            var Q20;
            Q20=makeQuery(id+"F9.opExtrude","CAP_EDGE",EDGE,{"disambiguationData":[OSD([sQuery(id+"F5.wireOp",EDGE,"E17.2.12")])],"isStart":true});
            var Q21;
            Q21=makeQuery(id+"F9.opExtrude","CAP_EDGE",EDGE,{"disambiguationData":[OSD([sQuery(id+"F5.wireOp",EDGE,"E17.2.9")])],"isStart":false});
            var Q22;
            Q22=makeQuery(id+"F9.opExtrude","CAP_EDGE",EDGE,{"disambiguationData":[OSD([sQuery(id+"F5.wireOp",EDGE,"E17.2.9")])],"isStart":true});
            var Q23;
            Q23=makeQuery(id+"F9.opExtrude","CAP_EDGE",EDGE,{"disambiguationData":[OSD([sQuery(id+"F5.wireOp",EDGE,"E17.2.18")])],"isStart":false});
            var Q24;
            Q24=makeQuery(id+"F9.opExtrude","CAP_EDGE",EDGE,{"disambiguationData":[OSD([sQuery(id+"F5.wireOp",EDGE,"E17.2.21")])],"isStart":false});
            var Q25;
            Q25=makeQuery(id+"F9.opExtrude","CAP_EDGE",EDGE,{"disambiguationData":[OSD([sQuery(id+"F5.wireOp",EDGE,"E17.1.9")])],"isStart":true});
            var Q26;
            Q26=makeQuery(id+"F9.opExtrude","CAP_EDGE",EDGE,{"disambiguationData":[OSD([sQuery(id+"F5.wireOp",EDGE,"E17.1.18")])],"isStart":true});
            var Q27;
            Q27=makeQuery(id+"F9.opExtrude","CAP_EDGE",EDGE,{"disambiguationData":[OSD([sQuery(id+"F5.wireOp",EDGE,"E17.2.21")])],"isStart":true});
            var Q28;
            Q28=makeQuery(id+"F9.opExtrude","CAP_EDGE",EDGE,{"disambiguationData":[OSD([sQuery(id+"F5.wireOp",EDGE,"E17.2.18")])],"isStart":true});
            var Q29;
            Q29=makeQuery(id+"F9.opExtrude","CAP_EDGE",EDGE,{"disambiguationData":[OSD([sQuery(id+"F5.wireOp",EDGE,"E17.3.21")])],"isStart":true});
            var Q30;
            Q30=makeQuery(id+"F9.opExtrude","CAP_EDGE",EDGE,{"disambiguationData":[OSD([sQuery(id+"F5.wireOp",EDGE,"E17.3.12")])],"isStart":true});
            var Q31;
            Q31=makeQuery(id+"F9.opExtrude","CAP_EDGE",EDGE,{"disambiguationData":[OSD([sQuery(id+"F5.wireOp",EDGE,"E17.1.21")])],"isStart":true});
            chamfer(context, id + "F10", {"entities" : qUnion([Q0, Q1, Q2, Q3, Q4, Q5, Q6, Q7, Q8, Q9, Q10, Q11, Q12, Q13, Q14, Q15, Q16, Q17, Q18, Q19, Q20, Q21, Q22, Q23, Q24, Q25, Q26, Q27, Q28, Q29, Q30, Q31]), "width" : 1 * mm, "tangentPropagation" : true});
        }
        {
            var Q0;
            Q0=makeQuery(id+"F5.imprint","IMPRINT",FACE,{"disambiguationData":[TD([[makeQuery(id+"F5.imprint","IMPRINT",EDGE,{"derivedFrom":sQuery(id+"F5.wireOp",EDGE,"E7.bottom")}),1.0]])]});
            var Q1;
            {var subQ1=sQuery(id+"F5.wireOp",EDGE,"E14.2.0");Q1=makeQuery(id+"F5.imprint","IMPRINT",FACE,{"disambiguationData":[TD([[makeQuery(id+"F5.imprint","IMPRINT",EDGE,{"derivedFrom":subQ1}),1.0]])]});}
            var Q2;
            {var subQ2=sQuery(id+"F5.wireOp",EDGE,"E12.2.0");Q2=makeQuery(id+"F5.imprint","IMPRINT",FACE,{"disambiguationData":[TD([[makeQuery(id+"F5.imprint","IMPRINT",EDGE,{"derivedFrom":subQ2}),1.0]])]});}
            var Q3;
            {var subQ1=sQuery(id+"F5.wireOp",EDGE,"E14.1.0");Q3=makeQuery(id+"F5.imprint","IMPRINT",FACE,{"disambiguationData":[TD([[makeQuery(id+"F5.imprint","IMPRINT",EDGE,{"derivedFrom":subQ1}),1.0]])]});}
            var Q4;
            {var subQ2=sQuery(id+"F5.wireOp",EDGE,"E12.1.0");Q4=makeQuery(id+"F5.imprint","IMPRINT",FACE,{"disambiguationData":[TD([[makeQuery(id+"F5.imprint","IMPRINT",EDGE,{"derivedFrom":subQ2}),1.0]])]});}
            var Q5;
            {var subQ2=sQuery(id+"F5.wireOp",EDGE,"E12.3.0");Q5=makeQuery(id+"F5.imprint","IMPRINT",FACE,{"disambiguationData":[TD([[makeQuery(id+"F5.imprint","IMPRINT",EDGE,{"derivedFrom":subQ2}),1.0]])]});}
            var Q6;
            {var subQ1=sQuery(id+"F5.wireOp",EDGE,"E14.3.0");Q6=makeQuery(id+"F5.imprint","IMPRINT",FACE,{"disambiguationData":[TD([[makeQuery(id+"F5.imprint","IMPRINT",EDGE,{"derivedFrom":subQ1}),1.0]])]});}
            var Q7;
            {var subQ2=sQuery(id+"F5.wireOp",EDGE,"E8.top");Q7=makeQuery(id+"F5.imprint","IMPRINT",FACE,{"disambiguationData":[TD([[makeQuery(id+"F5.imprint","IMPRINT",EDGE,{"derivedFrom":subQ2}),1.0]])]});}
            var Q8;
            {var subQ1=sQuery(id+"F5.wireOp",EDGE,"E13");Q8=makeQuery(id+"F5.imprint","IMPRINT",FACE,{"disambiguationData":[TD([[makeQuery(id+"F5.imprint","IMPRINT",EDGE,{"derivedFrom":subQ1}),1.0]])]});}
            var Q9;
            {var subQ2=sQuery(id+"F5.wireOp",EDGE,"E12.1.1");Q9=makeQuery(id+"F5.imprint","IMPRINT",FACE,{"disambiguationData":[TD([[makeQuery(id+"F5.imprint","IMPRINT",EDGE,{"derivedFrom":subQ2}),-1.0]])]});}
            var Q10;
            {var subQ2=sQuery(id+"F5.wireOp",EDGE,"E12.3.1");Q10=makeQuery(id+"F5.imprint","IMPRINT",FACE,{"disambiguationData":[TD([[makeQuery(id+"F5.imprint","IMPRINT",EDGE,{"derivedFrom":subQ2}),-1.0]])]});}
            var Q11;
            {var subQ2=sQuery(id+"F5.wireOp",EDGE,"E8.bottom");Q11=makeQuery(id+"F5.imprint","IMPRINT",FACE,{"disambiguationData":[TD([[makeQuery(id+"F5.imprint","IMPRINT",EDGE,{"derivedFrom":subQ2}),-1.0]])]});}
            var Q12;
            {var subQ2=sQuery(id+"F5.wireOp",EDGE,"E12.2.1");Q12=makeQuery(id+"F5.imprint","IMPRINT",FACE,{"disambiguationData":[TD([[makeQuery(id+"F5.imprint","IMPRINT",EDGE,{"derivedFrom":subQ2}),-1.0]])]});}
            var Q13;
            {var subQ2=sQuery(id+"F5.wireOp",EDGE,"E17.3.20");Q13=makeQuery(id+"F5.imprint","IMPRINT",FACE,{"disambiguationData":[TD([[makeQuery(id+"F5.imprint","IMPRINT",EDGE,{"derivedFrom":subQ2}),1.0]])]});}
            var Q14;
            {var subQ2=sQuery(id+"F5.wireOp",EDGE,"E17.3.17");Q14=makeQuery(id+"F5.imprint","IMPRINT",FACE,{"disambiguationData":[TD([[makeQuery(id+"F5.imprint","IMPRINT",EDGE,{"derivedFrom":subQ2}),1.0]])]});}
            var Q15;
            {var subQ2=sQuery(id+"F5.wireOp",EDGE,"E17.3.1");Q15=makeQuery(id+"F5.imprint","IMPRINT",FACE,{"disambiguationData":[TD([[makeQuery(id+"F5.imprint","IMPRINT",EDGE,{"derivedFrom":subQ2}),-1.0]])]});}
            var Q16;
            {var subQ1=sQuery(id+"F5.wireOp",EDGE,"E17.3.14");Q16=makeQuery(id+"F5.imprint","IMPRINT",FACE,{"disambiguationData":[TD([[makeQuery(id+"F5.imprint","IMPRINT",EDGE,{"derivedFrom":subQ1}),1.0]])]});}
            var Q17;
            {var subQ1=sQuery(id+"F5.wireOp",EDGE,"E17.3.18");Q17=makeQuery(id+"F5.imprint","IMPRINT",FACE,{"disambiguationData":[TD([[makeQuery(id+"F5.imprint","IMPRINT",EDGE,{"derivedFrom":subQ1}),-1.0]])]});}
            var Q18;
            {var subQ2=sQuery(id+"F5.wireOp",EDGE,"E17.3.11");Q18=makeQuery(id+"F5.imprint","IMPRINT",FACE,{"disambiguationData":[TD([[makeQuery(id+"F5.imprint","IMPRINT",EDGE,{"derivedFrom":subQ2}),-1.0]])]});}
            var Q19;
            {var subQ2=sQuery(id+"F5.wireOp",EDGE,"E17.3.4");Q19=makeQuery(id+"F5.imprint","IMPRINT",FACE,{"disambiguationData":[TD([[makeQuery(id+"F5.imprint","IMPRINT",EDGE,{"derivedFrom":subQ2}),1.0]])]});}
            var Q20;
            {var subQ2=sQuery(id+"F5.wireOp",EDGE,"E17.3.2");Q20=makeQuery(id+"F5.imprint","IMPRINT",FACE,{"disambiguationData":[TD([[makeQuery(id+"F5.imprint","IMPRINT",EDGE,{"derivedFrom":subQ2}),1.0]])]});}
            var Q21;
            {var subQ2=sQuery(id+"F5.wireOp",EDGE,"E17.3.4");Q21=makeQuery(id+"F5.imprint","IMPRINT",FACE,{"disambiguationData":[TD([[makeQuery(id+"F5.imprint","IMPRINT",EDGE,{"derivedFrom":subQ2}),-1.0]])]});}
            var Q22;
            {var subQ2=sQuery(id+"F5.wireOp",EDGE,"E17.3.3");Q22=makeQuery(id+"F5.imprint","IMPRINT",FACE,{"disambiguationData":[TD([[makeQuery(id+"F5.imprint","IMPRINT",EDGE,{"derivedFrom":subQ2}),1.0]])]});}
            var Q23;
            {var subQ2=sQuery(id+"F5.wireOp",EDGE,"E17.3.9");Q23=makeQuery(id+"F5.imprint","IMPRINT",FACE,{"disambiguationData":[TD([[makeQuery(id+"F5.imprint","IMPRINT",EDGE,{"derivedFrom":subQ2}),1.0]])]});}
            var Q24;
            {var subQ1=sQuery(id+"F5.wireOp",EDGE,"E17.3.22");Q24=makeQuery(id+"F5.imprint","IMPRINT",FACE,{"disambiguationData":[TD([[makeQuery(id+"F5.imprint","IMPRINT",EDGE,{"derivedFrom":subQ1}),-1.0]])]});}
            var Q25;
            {var subQ2=sQuery(id+"F5.wireOp",EDGE,"E17.2.22");Q25=makeQuery(id+"F5.imprint","IMPRINT",FACE,{"disambiguationData":[TD([[makeQuery(id+"F5.imprint","IMPRINT",EDGE,{"derivedFrom":subQ2}),-1.0]])]});}
            var Q26;
            {var subQ2=sQuery(id+"F5.wireOp",EDGE,"E17.2.9");Q26=makeQuery(id+"F5.imprint","IMPRINT",FACE,{"disambiguationData":[TD([[makeQuery(id+"F5.imprint","IMPRINT",EDGE,{"derivedFrom":subQ2}),1.0]])]});}
            var Q27;
            {var subQ2=sQuery(id+"F5.wireOp",EDGE,"E17.2.3");Q27=makeQuery(id+"F5.imprint","IMPRINT",FACE,{"disambiguationData":[TD([[makeQuery(id+"F5.imprint","IMPRINT",EDGE,{"derivedFrom":subQ2}),1.0]])]});}
            var Q28;
            {var subQ2=sQuery(id+"F5.wireOp",EDGE,"E17.2.11");Q28=makeQuery(id+"F5.imprint","IMPRINT",FACE,{"disambiguationData":[TD([[makeQuery(id+"F5.imprint","IMPRINT",EDGE,{"derivedFrom":subQ2}),-1.0]])]});}
            var Q29;
            {var subQ1=sQuery(id+"F5.wireOp",EDGE,"E17.2.14");Q29=makeQuery(id+"F5.imprint","IMPRINT",FACE,{"disambiguationData":[TD([[makeQuery(id+"F5.imprint","IMPRINT",EDGE,{"derivedFrom":subQ1}),1.0]])]});}
            var Q30;
            {var subQ1=sQuery(id+"F5.wireOp",EDGE,"E17.2.18");Q30=makeQuery(id+"F5.imprint","IMPRINT",FACE,{"disambiguationData":[TD([[makeQuery(id+"F5.imprint","IMPRINT",EDGE,{"derivedFrom":subQ1}),-1.0]])]});}
            var Q31;
            {var subQ2=sQuery(id+"F5.wireOp",EDGE,"E17.2.1");Q31=makeQuery(id+"F5.imprint","IMPRINT",FACE,{"disambiguationData":[TD([[makeQuery(id+"F5.imprint","IMPRINT",EDGE,{"derivedFrom":subQ2}),-1.0]])]});}
            var Q32;
            {var subQ2=sQuery(id+"F5.wireOp",EDGE,"E17.2.20");Q32=makeQuery(id+"F5.imprint","IMPRINT",FACE,{"disambiguationData":[TD([[makeQuery(id+"F5.imprint","IMPRINT",EDGE,{"derivedFrom":subQ2}),1.0]])]});}
            var Q33;
            {var subQ2=sQuery(id+"F5.wireOp",EDGE,"E17.2.17");Q33=makeQuery(id+"F5.imprint","IMPRINT",FACE,{"disambiguationData":[TD([[makeQuery(id+"F5.imprint","IMPRINT",EDGE,{"derivedFrom":subQ2}),1.0]])]});}
            var Q34;
            {var subQ2=sQuery(id+"F5.wireOp",EDGE,"E17.2.4");Q34=makeQuery(id+"F5.imprint","IMPRINT",FACE,{"disambiguationData":[TD([[makeQuery(id+"F5.imprint","IMPRINT",EDGE,{"derivedFrom":subQ2}),-1.0]])]});}
            var Q35;
            {var subQ2=sQuery(id+"F5.wireOp",EDGE,"E17.2.4");Q35=makeQuery(id+"F5.imprint","IMPRINT",FACE,{"disambiguationData":[TD([[makeQuery(id+"F5.imprint","IMPRINT",EDGE,{"derivedFrom":subQ2}),1.0]])]});}
            var Q36;
            {var subQ2=sQuery(id+"F5.wireOp",EDGE,"E17.2.2");Q36=makeQuery(id+"F5.imprint","IMPRINT",FACE,{"disambiguationData":[TD([[makeQuery(id+"F5.imprint","IMPRINT",EDGE,{"derivedFrom":subQ2}),1.0]])]});}
            var Q37;
            {var subQ2=sQuery(id+"F5.wireOp",EDGE,"E17.1.4");Q37=makeQuery(id+"F5.imprint","IMPRINT",FACE,{"disambiguationData":[TD([[makeQuery(id+"F5.imprint","IMPRINT",EDGE,{"derivedFrom":subQ2}),1.0]])]});}
            var Q38;
            {var subQ2=sQuery(id+"F5.wireOp",EDGE,"E17.1.4");Q38=makeQuery(id+"F5.imprint","IMPRINT",FACE,{"disambiguationData":[TD([[makeQuery(id+"F5.imprint","IMPRINT",EDGE,{"derivedFrom":subQ2}),-1.0]])]});}
            var Q39;
            {var subQ2=sQuery(id+"F5.wireOp",EDGE,"E17.1.2");Q39=makeQuery(id+"F5.imprint","IMPRINT",FACE,{"disambiguationData":[TD([[makeQuery(id+"F5.imprint","IMPRINT",EDGE,{"derivedFrom":subQ2}),1.0]])]});}
            var Q40;
            {var subQ2=sQuery(id+"F5.wireOp",EDGE,"E17.1.22");Q40=makeQuery(id+"F5.imprint","IMPRINT",FACE,{"disambiguationData":[TD([[makeQuery(id+"F5.imprint","IMPRINT",EDGE,{"derivedFrom":subQ2}),-1.0]])]});}
            var Q41;
            {var subQ2=sQuery(id+"F5.wireOp",EDGE,"E17.1.9");Q41=makeQuery(id+"F5.imprint","IMPRINT",FACE,{"disambiguationData":[TD([[makeQuery(id+"F5.imprint","IMPRINT",EDGE,{"derivedFrom":subQ2}),1.0]])]});}
            var Q42;
            {var subQ2=sQuery(id+"F5.wireOp",EDGE,"E17.1.3");Q42=makeQuery(id+"F5.imprint","IMPRINT",FACE,{"disambiguationData":[TD([[makeQuery(id+"F5.imprint","IMPRINT",EDGE,{"derivedFrom":subQ2}),1.0]])]});}
            var Q43;
            {var subQ2=sQuery(id+"F5.wireOp",EDGE,"E17.1.11");Q43=makeQuery(id+"F5.imprint","IMPRINT",FACE,{"disambiguationData":[TD([[makeQuery(id+"F5.imprint","IMPRINT",EDGE,{"derivedFrom":subQ2}),-1.0]])]});}
            var Q44;
            {var subQ2=sQuery(id+"F5.wireOp",EDGE,"E17.1.14");Q44=makeQuery(id+"F5.imprint","IMPRINT",FACE,{"disambiguationData":[TD([[makeQuery(id+"F5.imprint","IMPRINT",EDGE,{"derivedFrom":subQ2}),1.0]])]});}
            var Q45;
            {var subQ1=sQuery(id+"F5.wireOp",EDGE,"E17.1.18");Q45=makeQuery(id+"F5.imprint","IMPRINT",FACE,{"disambiguationData":[TD([[makeQuery(id+"F5.imprint","IMPRINT",EDGE,{"derivedFrom":subQ1}),-1.0]])]});}
            var Q46;
            {var subQ2=sQuery(id+"F5.wireOp",EDGE,"E17.1.20");Q46=makeQuery(id+"F5.imprint","IMPRINT",FACE,{"disambiguationData":[TD([[makeQuery(id+"F5.imprint","IMPRINT",EDGE,{"derivedFrom":subQ2}),1.0]])]});}
            var Q47;
            {var subQ2=sQuery(id+"F5.wireOp",EDGE,"E17.1.17");Q47=makeQuery(id+"F5.imprint","IMPRINT",FACE,{"disambiguationData":[TD([[makeQuery(id+"F5.imprint","IMPRINT",EDGE,{"derivedFrom":subQ2}),1.0]])]});}
            var Q48;
            {var subQ2=sQuery(id+"F5.wireOp",EDGE,"E17.1.1");Q48=makeQuery(id+"F5.imprint","IMPRINT",FACE,{"disambiguationData":[TD([[makeQuery(id+"F5.imprint","IMPRINT",EDGE,{"derivedFrom":subQ2}),-1.0]])]});}
            extrude(context, id + "F11", {"entities" : qUnion([Q0, Q1, Q2, Q3, Q4, Q5, Q6, Q7, Q8, Q9, Q10, Q11, Q12, Q13, Q14, Q15, Q16, Q17, Q18, Q19, Q20, Q21, Q22, Q23, Q24, Q25, Q26, Q27, Q28, Q29, Q30, Q31, Q32, Q33, Q34, Q35, Q36, Q37, Q38, Q39, Q40, Q41, Q42, Q43, Q44, Q45, Q46, Q47, Q48]), "oppositeDirection" : true, "depth" : 1 * mm});
        }
        {
            var Q0;
            Q0=makeQuery(id+"F0.imprint","IMPRINT",FACE,{"disambiguationData":[TD([[makeQuery(id+"F0.imprint","IMPRINT",EDGE,{"derivedFrom":sQuery(id+"F0.wireOp",EDGE,"E2")}),-1.0]])]});
            var Q1;
            Q1=makeQuery(id+"F0.imprint","IMPRINT",FACE,{"disambiguationData":[TD([[makeQuery(id+"F0.imprint","IMPRINT",EDGE,{"derivedFrom":sQuery(id+"F0.wireOp",EDGE,"E0.bottom")}),-1.0]])]});
            var Q2;
            Q2=makeQuery(id+"F0.imprint","IMPRINT",FACE,{"disambiguationData":[TD([[makeQuery(id+"F0.imprint","IMPRINT",EDGE,{"derivedFrom":sQuery(id+"F0.wireOp",EDGE,"E6.1.0")}),-1.0]])]});
            var Q3;
            Q3=makeQuery(id+"F0.imprint","IMPRINT",FACE,{"disambiguationData":[TD([[makeQuery(id+"F0.imprint","IMPRINT",EDGE,{"derivedFrom":sQuery(id+"F0.wireOp",EDGE,"E6.1.0")}),1.0]])]});
            var Q4;
            Q4=makeQuery(id+"F0.imprint","IMPRINT",FACE,{"disambiguationData":[TD([[makeQuery(id+"F0.imprint","IMPRINT",EDGE,{"derivedFrom":sQuery(id+"F0.wireOp",EDGE,"E1")}),1.0]])]});
            var Q5;
            Q5=makeQuery(id+"F0.imprint","IMPRINT",FACE,{"disambiguationData":[TD([[makeQuery(id+"F0.imprint","IMPRINT",EDGE,{"derivedFrom":sQuery(id+"F0.wireOp",EDGE,"E1")}),-1.0]])]});
            var Q6;
            Q6=makeQuery(id+"F0.imprint","IMPRINT",FACE,{"disambiguationData":[TD([[makeQuery(id+"F0.imprint","IMPRINT",EDGE,{"derivedFrom":sQuery(id+"F0.wireOp",EDGE,"E6.2.0")}),1.0]])]});
            var Q7;
            Q7=makeQuery(id+"F0.imprint","IMPRINT",FACE,{"disambiguationData":[TD([[makeQuery(id+"F0.imprint","IMPRINT",EDGE,{"derivedFrom":sQuery(id+"F0.wireOp",EDGE,"E6.2.0")}),-1.0]])]});
            var Q8;
            Q8=makeQuery(id+"F0.imprint","IMPRINT",FACE,{"disambiguationData":[TD([[makeQuery(id+"F0.imprint","IMPRINT",EDGE,{"derivedFrom":sQuery(id+"F0.wireOp",EDGE,"E6.3.0")}),1.0]])]});
            var Q9;
            Q9=makeQuery(id+"F0.imprint","IMPRINT",FACE,{"disambiguationData":[TD([[makeQuery(id+"F0.imprint","IMPRINT",EDGE,{"derivedFrom":sQuery(id+"F0.wireOp",EDGE,"E6.3.0")}),-1.0]])]});
            extrude(context, id + "F12", {"entities" : qUnion([Q0, Q1, Q2, Q3, Q4, Q5, Q6, Q7, Q8, Q9]), "oppositeDirection" : true, "depth" : 1 * mm});
        }
    });
